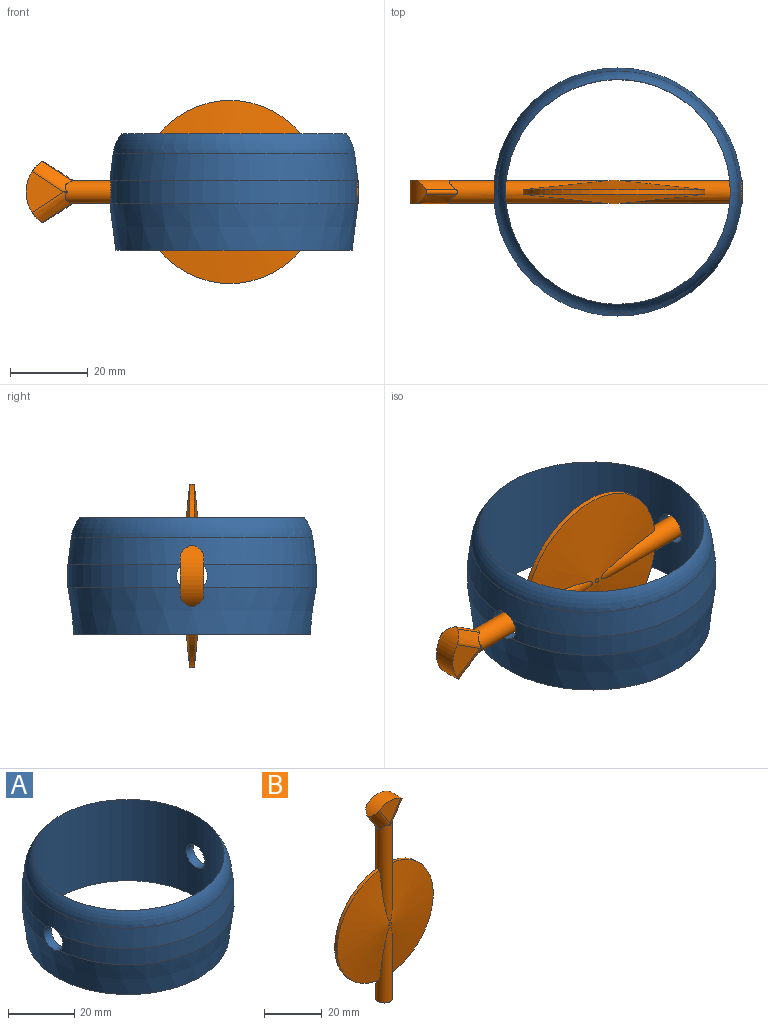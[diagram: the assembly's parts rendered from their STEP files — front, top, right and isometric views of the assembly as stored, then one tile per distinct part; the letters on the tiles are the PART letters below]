
ASSEMBLY  parts=2 mates=1
PART A: 9 faces, bbox 67.6x67.6x30.8 mm
  f0: cylinder r=32mm len=63.78mm, axis (0,0,-1), area 560.1mm2, adj f4,f5,f6,f7
  f1: cylinder r=29mm len=58mm, axis (0,0,-1), area 5365.4mm2, adj f3,f4,f5,f8
  f2: cylinder r=32mm len=63.78mm, axis (0,0,-1), area 560.1mm2, adj f4,f5,f6,f7
  f3: plane 61x61mm, normal (0,0,-1), area 280.4mm2, adj f1,f6
  f4: cylinder r=4mm len=8mm, axis (-1,0,0), area 74.8mm2, adj f0,f1,f2,f6,f7
  f5: cylinder r=4mm len=8mm, axis (-1,0,0), area 74.9mm2, adj f0,f1,f2,f6,f7
  f6: cone r=32mm half-angle=7.1deg, axis (0,0,1), area 2367.2mm2, adj f0,f2,f3,f4,f5
  f7: cone r=30.5mm half-angle=7.1deg, axis (0,0,-1), area 1387mm2, adj f0,f2,f4,f5,f8
  f8: torus R=21.21mm, axis (0,0,1), area 1051.9mm2, adj f1,f7
PART B: 22 faces, bbox 47.3x6x85.7 mm
  f0: cylinder r=2.9mm len=40.99mm, axis (0,0,-1), area 558.8mm2, adj f2,f3,f7,f9,f11,f12,f13,f14
  f1: cylinder r=2.9mm len=31.45mm, axis (0,0,-1), area 399.9mm2, adj f2,f3,f7,f9,f19
  f2: cylinder r=23.62mm len=46.91mm, axis (0,1,0), area 82.2mm2, adj f0,f1,f7,f9
  f3: cylinder r=23.62mm len=46.91mm, axis (0,1,0), area 82.2mm2, adj f0,f1,f7,f9
  f4: plane 1.25x1.25mm, normal (0,-1,0), area 1.2mm2, adj f7
  f5: cylinder r=9.5mm len=15.97mm, axis (0,1,0), area 93.9mm2, adj f6,f10,f11,f12,f13,f14,f16,f17
  f6: plane 10.48x9.74mm, normal (0,-1,0), area 54mm2, adj f5,f11,f12
  f7: cone r=0.62mm half-angle=84deg, axis (0,1,0), area 1572.1mm2, adj f0,f1,f2,f3,f4
  f8: plane 1.25x1.25mm, normal (0,1,0), area 1.2mm2, adj f9
  f9: cone r=0.62mm half-angle=84deg, axis (0,-1,0), area 1573.4mm2, adj f0,f1,f2,f3,f8
  f10: plane 10.48x9.74mm, normal (0,1,0), area 54mm2, adj f5,f13,f14
  f11: bspline ~10.52x8.51mm, area 40.2mm2, adj f0,f5,f6,f15,f16
  f12: bspline ~10.52x8.51mm, area 40.2mm2, adj f0,f5,f6,f15,f17
  f13: bspline ~10.52x8.51mm, area 40.2mm2, adj f0,f5,f10,f16,f18
  f14: bspline ~10.52x8.51mm, area 40.2mm2, adj f0,f5,f10,f17,f18
  f15: bspline ~0.94x0.64mm, area 0.2mm2, adj f0,f11,f12
  f16: bspline ~11.98x7.98mm, area 13.5mm2, adj f0,f5,f11,f13
  f17: bspline ~11.98x7.98mm, area 13.6mm2, adj f0,f5,f12,f14
  f18: bspline ~0.94x0.64mm, area 0.2mm2, adj f0,f13,f14
  f19: plane 5.8x5.8mm, normal (0,0,-1), area 13.9mm2, adj f1,f20
  f20: cylinder r=2mm len=20mm, axis (0,0,-1), area 251.3mm2, adj f19,f21
  f21: plane 4x4mm, normal (0,0,-1), area 12.6mm2, adj f20
PLACE A t=(-22.86,1.74,-16.41)mm
PLACE B rot(axis=(0,-1,0),90deg) t=(5.16,1.74,-1.41)mm
MATE slider B.f20 <-> A.f4  axis (1,0,0) through (9.16,1.74,-1.41)mm
